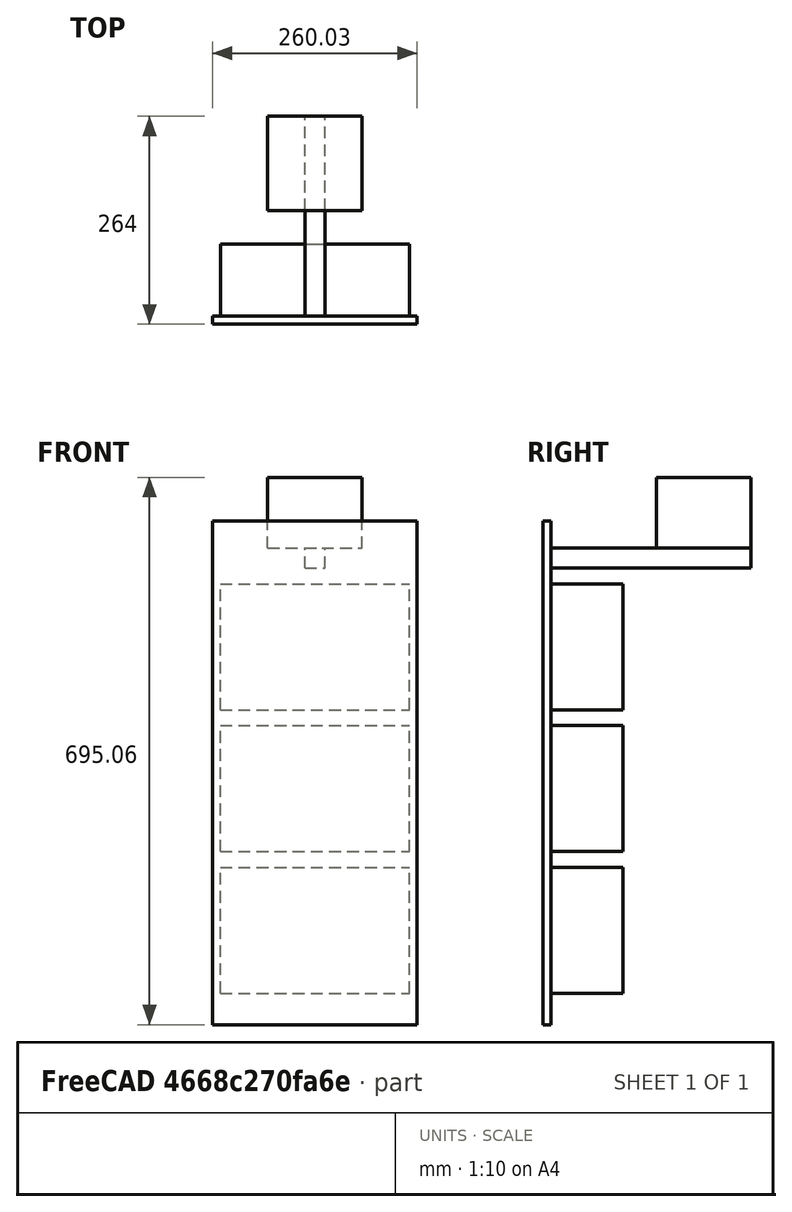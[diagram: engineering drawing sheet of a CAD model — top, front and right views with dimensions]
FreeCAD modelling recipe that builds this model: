
FCSTD DOCUMENT  (FreeCAD 0.17R13541 (Git))
Label: Latest
License: All rights reserved
LicenseURL: http://en.wikipedia.org/wiki/All_rights_reserved
objects: Part::Box×6
note: 6 computed .brp shape members not serialized (recipe doc carries the construction recipe); baked Part::Feature solids carry a one-line shape summary decoded from their .brp

FEATURE [Part::Box] Box  label="Power Module "
  AttacherType = Attacher::AttachEngine3D
  Height = 160.02
  Length = 240.03
  Width = 91.44
FEATURE [Part::Box] Box001  label="Main Module"
  AttacherType = Attacher::AttachEngine3D
  Height = 160.02
  Length = 240.03
  Placement = pos=(0,0,180) rot=(0,0,1;0rad)
  Width = 91.44
FEATURE [Part::Box] Box002  label="Ozone Module"
  AttacherType = Attacher::AttachEngine3D
  Height = 160.02
  Length = 240.03
  Placement = pos=(0,0,360) rot=(0,0,1;0rad)
  Width = 91.44
FEATURE [Part::Box] Box003  label="Light Module"
  AttacherType = Attacher::AttachEngine3D
  Height = 89.66
  Length = 119.89
  Placement = pos=(60.05,134.1,565.4) rot=(0,0,1;0rad)
  Width = 119.89
FEATURE [Part::Box] Box005  label="Railing"
  AttacherType = Attacher::AttachEngine3D
  Height = 25.4
  Length = 25.4
  Placement = pos=(107.3,0,540) rot=(0,0,1;0rad)
  Width = 254
FEATURE [Part::Box] Box006  label="BackPanel"
  AttacherType = Attacher::AttachEngine3D
  Height = 640
  Length = 260.03
  Placement = pos=(-10,-10,-40) rot=(0,0,1;0rad)
  Width = 10
